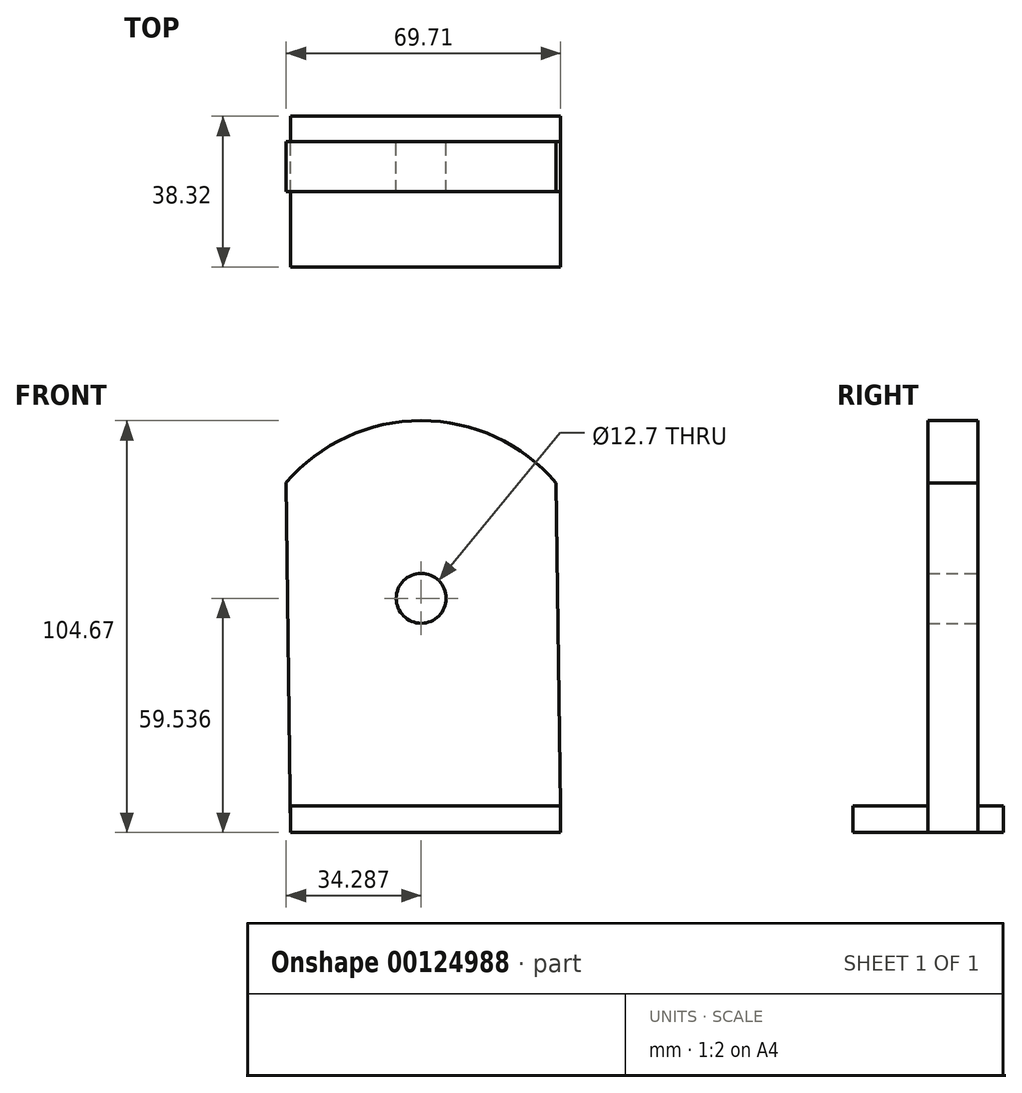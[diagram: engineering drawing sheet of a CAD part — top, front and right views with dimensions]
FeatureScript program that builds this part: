
annotation { "Feature Type Name" : "Feature", "Feature Type Description" : "" }
export const myFeature = defineFeature(function(context is Context, id is Id, definition is map)
    precondition{}
    {
        {
            var Q0;
            Q0=qCreatedBy(makeId("Front.planeOp"),FACE);
            var sketch = newSketch(context, id + "F0", { "sketchPlane" : qUnion([Q0])});
            skLineSegment(sketch, "E0.bottom", {"start": v(-48.34, -59.39) * mm, "end": v(20.24, -59.39) * mm});
            skLineSegment(sketch, "E0.left", {"start": v(-48.34, -59.39) * mm, "end": v(-49.47, 29.5) * mm});
            skLineSegment(sketch, "E0.right", {"start": v(20.24, -59.39) * mm, "end": v(19.11, 29.5) * mm});
            skArc(sketch, "E1", {"start": v(19.11, 29.5) * mm, "mid": v(-15.18, 45.28) * mm, "end": v(-49.47, 29.5) * mm});
            skCircle(sketch, "E2", {"center": v(-15.18, 0.15) * mm, "radius": 6.35 * mm});
            skSolve(sketch);
        }
        {
            var Q0;
            Q0=makeQuery(id+"F0.imprint","IMPRINT",FACE,{"disambiguationData":[TD([[makeQuery(id+"F0.imprint","IMPRINT",EDGE,{"derivedFrom":sQuery(id+"F0.wireOp",EDGE,"E0.bottom")}),1.0]])]});
            extrude(context, id + "F1", {"entities" : qUnion([Q0]), "depth" : 12.7 * mm});
        }
        {
            var Q0;
            Q0=makeQuery(id+"F1.opExtrude","CAP_FACE",FACE,{"disambiguationData":[OSD([sQuery(id+"F0.wireOp",EDGE,"E0.bottom"),sQuery(id+"F0.wireOp",EDGE,"E0.left"),sQuery(id+"F0.wireOp",EDGE,"E0.right"),sQuery(id+"F0.wireOp",EDGE,"E1"),sQuery(id+"F0.wireOp",EDGE,"E2")])],"isStart":false});
            var sketch = newSketch(context, id + "F2", { "sketchPlane" : qUnion([Q0])});
            skLineSegment(sketch, "E3.bottom", {"start": v(-48.34, -59.39) * mm, "end": v(20.16, -59.39) * mm});
            skLineSegment(sketch, "E3.top", {"start": v(-48.34, -52.64) * mm, "end": v(20.16, -52.64) * mm});
            skLineSegment(sketch, "E3.left", {"start": v(-48.34, -59.39) * mm, "end": v(-48.34, -52.64) * mm});
            skLineSegment(sketch, "E3.right", {"start": v(20.16, -59.39) * mm, "end": v(20.16, -52.64) * mm});
            skSolve(sketch);
        }
        {
            var Q0;
            Q0=makeQuery(id+"F2.imprint","IMPRINT",FACE,{"disambiguationData":[TD([[makeQuery(id+"F2.imprint","IMPRINT",EDGE,{"derivedFrom":sQuery(id+"F2.wireOp",EDGE,"E3.bottom")}),1.0]])]});
            extrude(context, id + "F3", {"entities" : qUnion([Q0]), "operationType" : NewBodyOperationType.ADD, "endBound" : BoundingType.SYMMETRIC, "oppositeDirection" : true, "depth" : 38.32 * mm});
        }
    });
